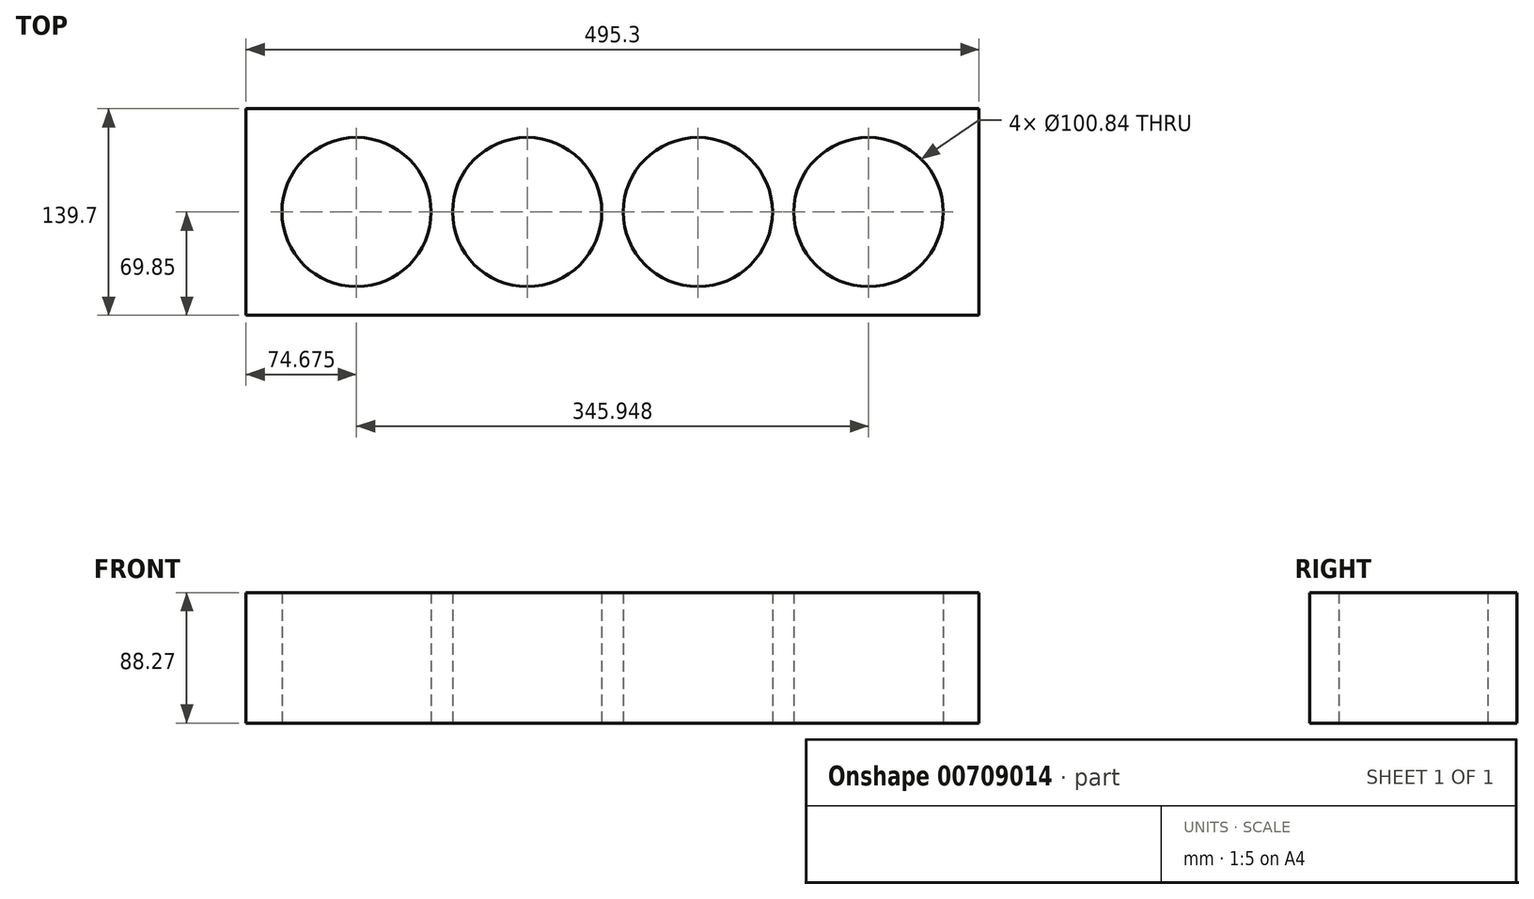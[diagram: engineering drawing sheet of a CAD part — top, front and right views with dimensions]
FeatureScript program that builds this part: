
annotation { "Feature Type Name" : "Feature", "Feature Type Description" : "" }
export const myFeature = defineFeature(function(context is Context, id is Id, definition is map)
    precondition{}
    {
        {
            var Q0;
            Q0=qCreatedBy(makeId("Top.planeOp"),FACE);
            var sketch = newSketch(context, id + "F0", { "sketchPlane" : qUnion([Q0])});
            skCircle(sketch, "E0", {"center": v(-159.05, 0) * mm, "radius": 50.42 * mm});
            skCircle(sketch, "E1.1.0.0", {"center": v(-43.74, 0) * mm, "radius": 50.42 * mm});
            skCircle(sketch, "E1.2.0.0", {"center": v(71.58, 0) * mm, "radius": 50.42 * mm});
            skCircle(sketch, "E1.3.0.0", {"center": v(186.9, 0) * mm, "radius": 50.42 * mm});
            skLineSegment(sketch, "E1.direction1", {"start": v(-159.05, 0) * mm, "end": v(-43.74, 0) * mm, "construction": true});
            skLineSegment(sketch, "E2", {"start": v(-159.05, 0) * mm, "end": v(186.9, 0) * mm, "construction": true});
            skLineSegment(sketch, "E3.bottom", {"start": v(261.57, 69.85) * mm, "end": v(-233.73, 69.85) * mm});
            skLineSegment(sketch, "E3.top", {"start": v(261.57, -69.85) * mm, "end": v(-233.73, -69.85) * mm});
            skLineSegment(sketch, "E3.left", {"start": v(261.57, 69.85) * mm, "end": v(261.57, -69.85) * mm});
            skLineSegment(sketch, "E3.right", {"start": v(-233.73, 69.85) * mm, "end": v(-233.73, -69.85) * mm});
            skPoint(sketch, "E3.middle", {"position": v(13.92, 0) * mm});
            skSolve(sketch);
        }
        {
            var Q0;
            Q0=makeQuery(id+"F0.imprint","IMPRINT",FACE,{"disambiguationData":[TD([[makeQuery(id+"F0.imprint","IMPRINT",EDGE,{"derivedFrom":sQuery(id+"F0.wireOp",EDGE,"E0")}),-1.0]])]});
            extrude(context, id + "F1", {"entities" : qUnion([Q0]), "depth" : 88.27 * mm, "offsetDistance" : 25.4 * mm});
        }
    });
